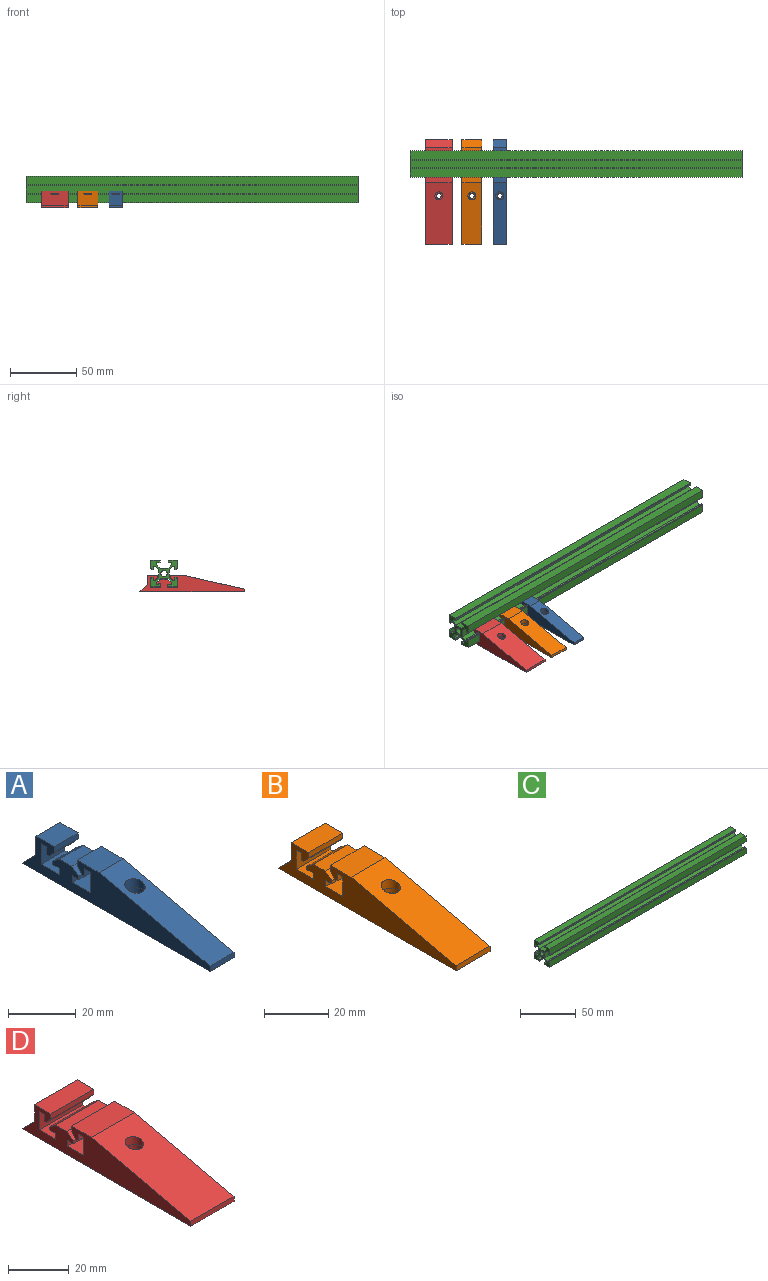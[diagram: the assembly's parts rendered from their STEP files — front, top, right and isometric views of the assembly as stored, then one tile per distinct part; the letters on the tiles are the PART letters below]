
ASSEMBLY  parts=4 mates=3
PART A: 37 faces, bbox 10x78.6x12.6 mm
  f0: plane 10x7.64mm, normal (0,0,1), area 76.4mm2, adj f1,f29,f30,f31
  f1: plane 10x2mm, normal (0,-1,0), area 20mm2, adj f0,f2,f30,f31
  f2: plane 10x2.38mm, normal (0,-0.76,-0.66), area 31.5mm2, adj f1,f3,f30,f31
  f3: plane 10x1.05mm, normal (0,0,-1), area 10.5mm2, adj f2,f4,f30,f31
  f4: plane 10x2.75mm, normal (0,1,0), area 27.5mm2, adj f3,f5,f30,f31
  f5: plane 10x2.39mm, normal (0,0,-1), area 23.9mm2, adj f4,f6,f30,f31
  f6: plane 10x7.45mm, normal (0,-1,0), area 74.5mm2, adj f5,f7,f30,f31
  f7: plane 10x7.6mm, normal (0,0,1), area 76mm2, adj f6,f8,f30,f31
  f8: plane 10x2.35mm, normal (0,1,0), area 23.5mm2, adj f7,f9,f30,f31
  f9: plane 10x2.82mm, normal (0,0,-1), area 28.2mm2, adj f8,f10,f30,f31
  f10: plane 10x1.15mm, normal (0,1,0), area 11.5mm2, adj f9,f11,f30,f31
  f11: plane 10x2.9mm, normal (0,0.61,0.79), area 36.6mm2, adj f10,f12,f30,f31
  f12: plane 10x5.2mm, normal (0,0,1), area 52mm2, adj f11,f13,f30,f31
  f13: plane 10x2.9mm, normal (0,-0.62,0.79), area 36.9mm2, adj f12,f14,f30,f31
  f14: plane 10x1.15mm, normal (0,-1,0), area 11.5mm2, adj f13,f15,f30,f31
  f15: plane 10x2.78mm, normal (0,0,-1), area 27.8mm2, adj f14,f16,f30,f31
  f16: plane 10x2.35mm, normal (0,-1,0), area 23.5mm2, adj f15,f17,f30,f31
  f17: plane 10x7.6mm, normal (0,0,1), area 76mm2, adj f16,f18,f30,f31
  f18: plane 10x7.45mm, normal (0,1,0), area 74.5mm2, adj f17,f19,f30,f31
  f19: plane 10x2.5mm, normal (0,0,-1), area 25mm2, adj f18,f20,f30,f31
  f20: plane 10x2.75mm, normal (0,-1,0), area 27.5mm2, adj f19,f21,f30,f31
  f21: plane 10x1.05mm, normal (0,0,-1), area 10.5mm2, adj f20,f22,f30,f31
  f22: plane 10x2.43mm, normal (0,0.79,-0.61), area 30.8mm2, adj f21,f23,f30,f31
  f23: plane 10x2mm, normal (0,1,0), area 20mm2, adj f22,f24,f30,f31
  f24: plane 10x9.11mm, normal (0,0,1), area 91.1mm2, adj f23,f25,f30,f31
  f25: plane 46.33x10.6mm, normal (0,-0.22,0.97), area 446.3mm2, adj f24,f26,f30,f31,f32
  f26: plane 10x2mm, normal (0,-1,0), area 20mm2, adj f25,f27,f30,f31
  f27: plane 78.55x10mm, normal (0,0,-1), area 775.4mm2, adj f26,f28,f30,f31,f34
  f28: plane 10x5.82mm, normal (0,0.71,0.71), area 82.3mm2, adj f27,f29,f30,f31
  f29: plane 10x6.78mm, normal (0,1,0), area 67.8mm2, adj f0,f28,f30,f31
  f30: plane 78.55x12.6mm, normal (1,0,0), area 573.8mm2, adj f0,f1,f2,f3,f4,f5,f6,f7
  f31: plane 78.55x12.6mm, normal (-1,0,0), area 573.8mm2, adj f0,f1,f2,f3,f4,f5,f6,f7
  f32: cylinder r=3mm len=6mm, axis (0,0,-1), area 51.1mm2, adj f25,f33
  f33: plane 6.5x6.5mm, normal (0,0,-1), area 4.9mm2, adj f32,f36
  f34: cylinder r=1.8mm len=5.6mm, axis (0,0,1), area 63.3mm2, adj f27,f35
  f35: plane 6.5x6.5mm, normal (0,0,1), area 23mm2, adj f34,f36
  f36: cylinder r=3.25mm len=6.5mm, axis (0,0,1), area 40.8mm2, adj f33,f35
PART B: 37 faces, bbox 15x78.6x12.6 mm
  f0: plane 15x7.64mm, normal (0,0,1), area 114.6mm2, adj f1,f29,f30,f31
  f1: plane 15x2mm, normal (0,-1,0), area 30mm2, adj f0,f2,f30,f31
  f2: plane 15x2.38mm, normal (0,-0.76,-0.66), area 47.2mm2, adj f1,f3,f30,f31
  f3: plane 15x1.05mm, normal (0,0,-1), area 15.8mm2, adj f2,f4,f30,f31
  f4: plane 15x2.75mm, normal (0,1,0), area 41.2mm2, adj f3,f5,f30,f31
  f5: plane 15x2.39mm, normal (0,0,-1), area 35.9mm2, adj f4,f6,f30,f31
  f6: plane 15x7.45mm, normal (0,-1,0), area 111.7mm2, adj f5,f7,f30,f31
  f7: plane 15x7.6mm, normal (0,0,1), area 114mm2, adj f6,f8,f30,f31
  f8: plane 15x2.35mm, normal (0,1,0), area 35.2mm2, adj f7,f9,f30,f31
  f9: plane 15x2.82mm, normal (0,0,-1), area 42.2mm2, adj f8,f10,f30,f31
  f10: plane 15x1.15mm, normal (0,1,0), area 17.3mm2, adj f9,f11,f30,f31
  f11: plane 15x2.9mm, normal (0,0.61,0.79), area 54.9mm2, adj f10,f12,f30,f31
  f12: plane 15x5.2mm, normal (0,0,1), area 78mm2, adj f11,f13,f30,f31
  f13: plane 15x2.9mm, normal (0,-0.62,0.79), area 55.3mm2, adj f12,f14,f30,f31
  f14: plane 15x1.15mm, normal (0,-1,0), area 17.3mm2, adj f13,f15,f30,f31
  f15: plane 15x2.78mm, normal (0,0,-1), area 41.8mm2, adj f14,f16,f30,f31
  f16: plane 15x2.35mm, normal (0,-1,0), area 35.3mm2, adj f15,f17,f30,f31
  f17: plane 15x7.6mm, normal (0,0,1), area 114mm2, adj f16,f18,f30,f31
  f18: plane 15x7.45mm, normal (0,1,0), area 111.7mm2, adj f17,f19,f30,f31
  f19: plane 15x2.5mm, normal (0,0,-1), area 37.6mm2, adj f18,f20,f30,f31
  f20: plane 15x2.75mm, normal (0,-1,0), area 41.2mm2, adj f19,f21,f30,f31
  f21: plane 15x1.05mm, normal (0,0,-1), area 15.8mm2, adj f20,f22,f30,f31
  f22: plane 15x2.43mm, normal (0,0.79,-0.61), area 46.1mm2, adj f21,f23,f30,f31
  f23: plane 15x2mm, normal (0,1,0), area 30mm2, adj f22,f24,f30,f31
  f24: plane 15x9.11mm, normal (0,0,1), area 136.7mm2, adj f23,f25,f30,f31
  f25: plane 46.33x15mm, normal (0,-0.22,0.97), area 683.9mm2, adj f24,f26,f30,f31,f32
  f26: plane 15x2mm, normal (0,-1,0), area 30mm2, adj f25,f27,f30,f31
  f27: plane 78.55x15mm, normal (0,0,-1), area 1168.1mm2, adj f26,f28,f30,f31,f34
  f28: plane 15x5.82mm, normal (0,0.71,0.71), area 123.5mm2, adj f27,f29,f30,f31
  f29: plane 15x6.78mm, normal (0,1,0), area 101.7mm2, adj f0,f28,f30,f31
  f30: plane 78.55x12.6mm, normal (1,0,0), area 573.8mm2, adj f0,f1,f2,f3,f4,f5,f6,f7
  f31: plane 78.55x12.6mm, normal (-1,0,0), area 573.8mm2, adj f0,f1,f2,f3,f4,f5,f6,f7
  f32: cylinder r=3mm len=6mm, axis (0,0,-1), area 51.1mm2, adj f25,f33
  f33: plane 6.5x6.5mm, normal (0,0,-1), area 4.9mm2, adj f32,f36
  f34: cylinder r=1.8mm len=5.6mm, axis (0,0,1), area 63.3mm2, adj f27,f35
  f35: plane 6.5x6.5mm, normal (0,0,1), area 23mm2, adj f34,f36
  f36: cylinder r=3.25mm len=6.5mm, axis (0,0,1), area 40.8mm2, adj f33,f35
PART C: 63 faces, bbox 250x20x20 mm
  f0: plane 250x1.64mm, normal (0,0,-1), area 409.8mm2, adj f1,f59,f61,f62
  f1: plane 250x2.5mm, normal (0,-1,0), area 625mm2, adj f0,f2,f61,f62
  f2: plane 250x1.3mm, normal (0,0,-1), area 325mm2, adj f1,f3,f61,f62
  f3: plane 250x0.5mm, normal (0,1,0), area 125mm2, adj f2,f4,f61,f62
  f4: plane 250x0.5mm, normal (0,0,-1), area 125mm2, adj f3,f5,f61,f62
  f5: plane 250x6.5mm, normal (0,1,0), area 1625mm2, adj f4,f6,f61,f62
  f6: plane 250x6.5mm, normal (0,0,1), area 1625mm2, adj f5,f7,f61,f62
  f7: plane 250x0.5mm, normal (0,-1,0), area 125mm2, adj f6,f8,f61,f62
  f8: plane 250x0.5mm, normal (0,0,1), area 125mm2, adj f7,f9,f61,f62
  f9: plane 250x1.3mm, normal (0,-1,0), area 325mm2, adj f8,f10,f61,f62
  f10: plane 250x2.5mm, normal (0,0,-1), area 625mm2, adj f9,f11,f61,f62
  f11: plane 250x1.64mm, normal (0,-1,0), area 409.8mm2, adj f10,f12,f61,f62
  f12: plane 250x2.56mm, normal (0,-0.71,0.71), area 905.3mm2, adj f11,f13,f61,f62
  f13: plane 250x5.88mm, normal (0,0,1), area 1469.7mm2, adj f12,f14,f61,f62
  f14: plane 250x2.56mm, normal (0,0.71,0.71), area 905.3mm2, adj f13,f15,f61,f62
  f15: plane 250x1.64mm, normal (0,1,0), area 409.8mm2, adj f14,f16,f61,f62
  f16: plane 250x2.5mm, normal (0,0,-1), area 625mm2, adj f15,f17,f61,f62
  f17: plane 250x1.3mm, normal (0,1,0), area 325mm2, adj f16,f18,f61,f62
  f18: plane 250x0.5mm, normal (0,0,1), area 125mm2, adj f17,f19,f61,f62
  f19: plane 250x0.5mm, normal (0,1,0), area 125mm2, adj f18,f20,f61,f62
  f20: plane 250x6.5mm, normal (0,0,1), area 1625mm2, adj f19,f21,f61,f62
  f21: plane 250x6.5mm, normal (0,-1,0), area 1625mm2, adj f20,f22,f61,f62
  f22: plane 250x0.5mm, normal (0,0,-1), area 125mm2, adj f21,f23,f61,f62
  f23: plane 250x0.5mm, normal (0,-1,0), area 125mm2, adj f22,f24,f61,f62
  f24: plane 250x1.3mm, normal (0,0,-1), area 325mm2, adj f23,f25,f61,f62
  f25: plane 250x2.5mm, normal (0,1,0), area 625mm2, adj f24,f26,f61,f62
  f26: plane 250x1.64mm, normal (0,0,-1), area 409.8mm2, adj f25,f27,f61,f62
  f27: plane 250x2.56mm, normal (0,-0.71,-0.71), area 905.3mm2, adj f26,f28,f61,f62
  f28: plane 250x5.88mm, normal (0,-1,0), area 1469.7mm2, adj f27,f29,f61,f62
  f29: plane 250x2.56mm, normal (0,-0.71,0.71), area 905.3mm2, adj f28,f30,f61,f62
  f30: plane 250x1.64mm, normal (0,0,1), area 409.8mm2, adj f29,f31,f61,f62
  f31: plane 250x2.5mm, normal (0,1,0), area 625mm2, adj f30,f32,f61,f62
  f32: plane 250x1.3mm, normal (0,0,1), area 325mm2, adj f31,f33,f61,f62
  f33: plane 250x0.5mm, normal (0,-1,0), area 125mm2, adj f32,f34,f61,f62
  f34: plane 250x0.5mm, normal (0,0,1), area 125mm2, adj f33,f35,f61,f62
  f35: plane 250x6.5mm, normal (0,-1,0), area 1625mm2, adj f34,f36,f61,f62
  f36: plane 250x6.5mm, normal (0,0,-1), area 1625mm2, adj f35,f37,f61,f62
  f37: plane 250x0.5mm, normal (0,1,0), area 125mm2, adj f36,f38,f61,f62
  f38: plane 250x0.5mm, normal (0,0,-1), area 125mm2, adj f37,f39,f61,f62
  f39: plane 250x1.3mm, normal (0,1,0), area 325mm2, adj f38,f40,f61,f62
  f40: plane 250x2.5mm, normal (0,0,1), area 625mm2, adj f39,f41,f61,f62
  f41: plane 250x1.64mm, normal (0,1,0), area 409.8mm2, adj f40,f42,f61,f62
  f42: plane 250x2.56mm, normal (0,0.71,-0.71), area 905.3mm2, adj f41,f43,f61,f62
  f43: plane 250x5.88mm, normal (0,0,-1), area 1469.7mm2, adj f42,f44,f61,f62
  f44: plane 250x2.56mm, normal (0,-0.71,-0.71), area 905.3mm2, adj f43,f45,f61,f62
  f45: plane 250x1.64mm, normal (0,-1,0), area 409.8mm2, adj f44,f46,f61,f62
  f46: plane 250x2.5mm, normal (0,0,1), area 625mm2, adj f45,f47,f61,f62
  f47: plane 250x1.3mm, normal (0,-1,0), area 325mm2, adj f46,f48,f61,f62
  f48: plane 250x0.5mm, normal (0,0,-1), area 125mm2, adj f47,f49,f61,f62
  f49: plane 250x0.5mm, normal (0,-1,0), area 125mm2, adj f48,f50,f61,f62
  f50: plane 250x6.5mm, normal (0,0,-1), area 1625mm2, adj f49,f51,f61,f62
  f51: plane 250x6.5mm, normal (0,1,0), area 1625mm2, adj f50,f52,f61,f62
  f52: plane 250x0.5mm, normal (0,0,1), area 125mm2, adj f51,f53,f61,f62
  f53: plane 250x0.5mm, normal (0,1,0), area 125mm2, adj f52,f54,f61,f62
  f54: plane 250x1.3mm, normal (0,0,1), area 325mm2, adj f53,f55,f61,f62
  f55: plane 250x2.5mm, normal (0,-1,0), area 625mm2, adj f54,f56,f61,f62
  f56: plane 250x1.64mm, normal (0,0,1), area 409.8mm2, adj f55,f57,f61,f62
  f57: plane 250x2.56mm, normal (0,0.71,0.71), area 905.3mm2, adj f56,f58,f61,f62
  f58: plane 250x5.88mm, normal (0,1,0), area 1469.7mm2, adj f57,f59,f61,f62
  f59: plane 250x2.56mm, normal (0,0.71,-0.71), area 905.3mm2, adj f0,f58,f61,f62
  f60: cylinder r=2.4mm len=250mm, axis (-1,0,0), area 3769.9mm2, adj f61,f62
  f61: plane 20x20mm, normal (1,0,0), area 178.1mm2, adj f0,f1,f2,f3,f4,f5,f6,f7
  f62: plane 20x20mm, normal (-1,0,0), area 178.1mm2, adj f0,f1,f2,f3,f4,f5,f6,f7
PART D: 37 faces, bbox 20x78.6x12.6 mm
  f0: plane 20x7.64mm, normal (0,0,1), area 152.9mm2, adj f1,f29,f30,f31
  f1: plane 20x2mm, normal (0,-1,0), area 40mm2, adj f0,f2,f30,f31
  f2: plane 20x2.38mm, normal (0,-0.76,-0.66), area 63mm2, adj f1,f3,f30,f31
  f3: plane 20x1.05mm, normal (0,0,-1), area 21mm2, adj f2,f4,f30,f31
  f4: plane 20x2.75mm, normal (0,1,0), area 55mm2, adj f3,f5,f30,f31
  f5: plane 20x2.39mm, normal (0,0,-1), area 47.9mm2, adj f4,f6,f30,f31
  f6: plane 20x7.45mm, normal (0,-1,0), area 149mm2, adj f5,f7,f30,f31
  f7: plane 20x7.6mm, normal (0,0,1), area 152mm2, adj f6,f8,f30,f31
  f8: plane 20x2.35mm, normal (0,1,0), area 47mm2, adj f7,f9,f30,f31
  f9: plane 20x2.82mm, normal (0,0,-1), area 56.3mm2, adj f8,f10,f30,f31
  f10: plane 20x1.15mm, normal (0,1,0), area 23mm2, adj f9,f11,f30,f31
  f11: plane 20x2.9mm, normal (0,0.61,0.79), area 73.1mm2, adj f10,f12,f30,f31
  f12: plane 20x5.2mm, normal (0,0,1), area 104mm2, adj f11,f13,f30,f31
  f13: plane 20x2.9mm, normal (0,-0.62,0.79), area 73.8mm2, adj f12,f14,f30,f31
  f14: plane 20x1.15mm, normal (0,-1,0), area 23mm2, adj f13,f15,f30,f31
  f15: plane 20x2.78mm, normal (0,0,-1), area 55.7mm2, adj f14,f16,f30,f31
  f16: plane 20x2.35mm, normal (0,-1,0), area 47mm2, adj f15,f17,f30,f31
  f17: plane 20x7.6mm, normal (0,0,1), area 151.9mm2, adj f16,f18,f30,f31
  f18: plane 20x7.45mm, normal (0,1,0), area 149mm2, adj f17,f19,f30,f31
  f19: plane 20x2.5mm, normal (0,0,-1), area 50.1mm2, adj f18,f20,f30,f31
  f20: plane 20x2.75mm, normal (0,-1,0), area 55mm2, adj f19,f21,f30,f31
  f21: plane 20x1.05mm, normal (0,0,-1), area 21mm2, adj f20,f22,f30,f31
  f22: plane 20x2.43mm, normal (0,0.79,-0.61), area 61.5mm2, adj f21,f23,f30,f31
  f23: plane 20x2mm, normal (0,1,0), area 40mm2, adj f22,f24,f30,f31
  f24: plane 20x9.11mm, normal (0,0,1), area 182.2mm2, adj f23,f25,f30,f31
  f25: plane 46.33x20mm, normal (0,-0.22,0.97), area 921.6mm2, adj f24,f26,f30,f31,f32
  f26: plane 20x2mm, normal (0,-1,0), area 40mm2, adj f25,f27,f30,f31
  f27: plane 78.55x20mm, normal (0,0,-1), area 1560.9mm2, adj f26,f28,f30,f31,f34
  f28: plane 20x5.82mm, normal (0,0.71,0.71), area 164.6mm2, adj f27,f29,f30,f31
  f29: plane 20x6.78mm, normal (0,1,0), area 135.6mm2, adj f0,f28,f30,f31
  f30: plane 78.55x12.6mm, normal (1,0,0), area 573.8mm2, adj f0,f1,f2,f3,f4,f5,f6,f7
  f31: plane 78.55x12.6mm, normal (-1,0,0), area 573.8mm2, adj f0,f1,f2,f3,f4,f5,f6,f7
  f32: cylinder r=3mm len=6mm, axis (0,0,-1), area 51.1mm2, adj f25,f33
  f33: plane 6.5x6.5mm, normal (0,0,-1), area 4.9mm2, adj f32,f36
  f34: cylinder r=1.8mm len=5.6mm, axis (0,0,1), area 63.3mm2, adj f27,f35
  f35: plane 6.5x6.5mm, normal (0,0,1), area 23mm2, adj f34,f36
  f36: cylinder r=3.25mm len=6.5mm, axis (0,0,1), area 40.8mm2, adj f33,f35
PLACE A rot(axis=(1,0,0),0deg) t=(-57.4,-6.21,-7.93)mm
PLACE B t=(-78.43,-6.21,-7.93)mm
PLACE C at identity fixed
PLACE D t=(-103.32,-6.21,-7.93)mm
MATE slider D.f31 <-> C.f62  axis (-1,0,0) through (-113.32,0,-4.5)mm
MATE slider C.f62 <-> A.f31  axis (-1,0,0) through (-125,0,-4.5)mm
MATE slider B.f31 <-> C.f62  axis (-1,0,0) through (-85.93,0,-4.5)mm
